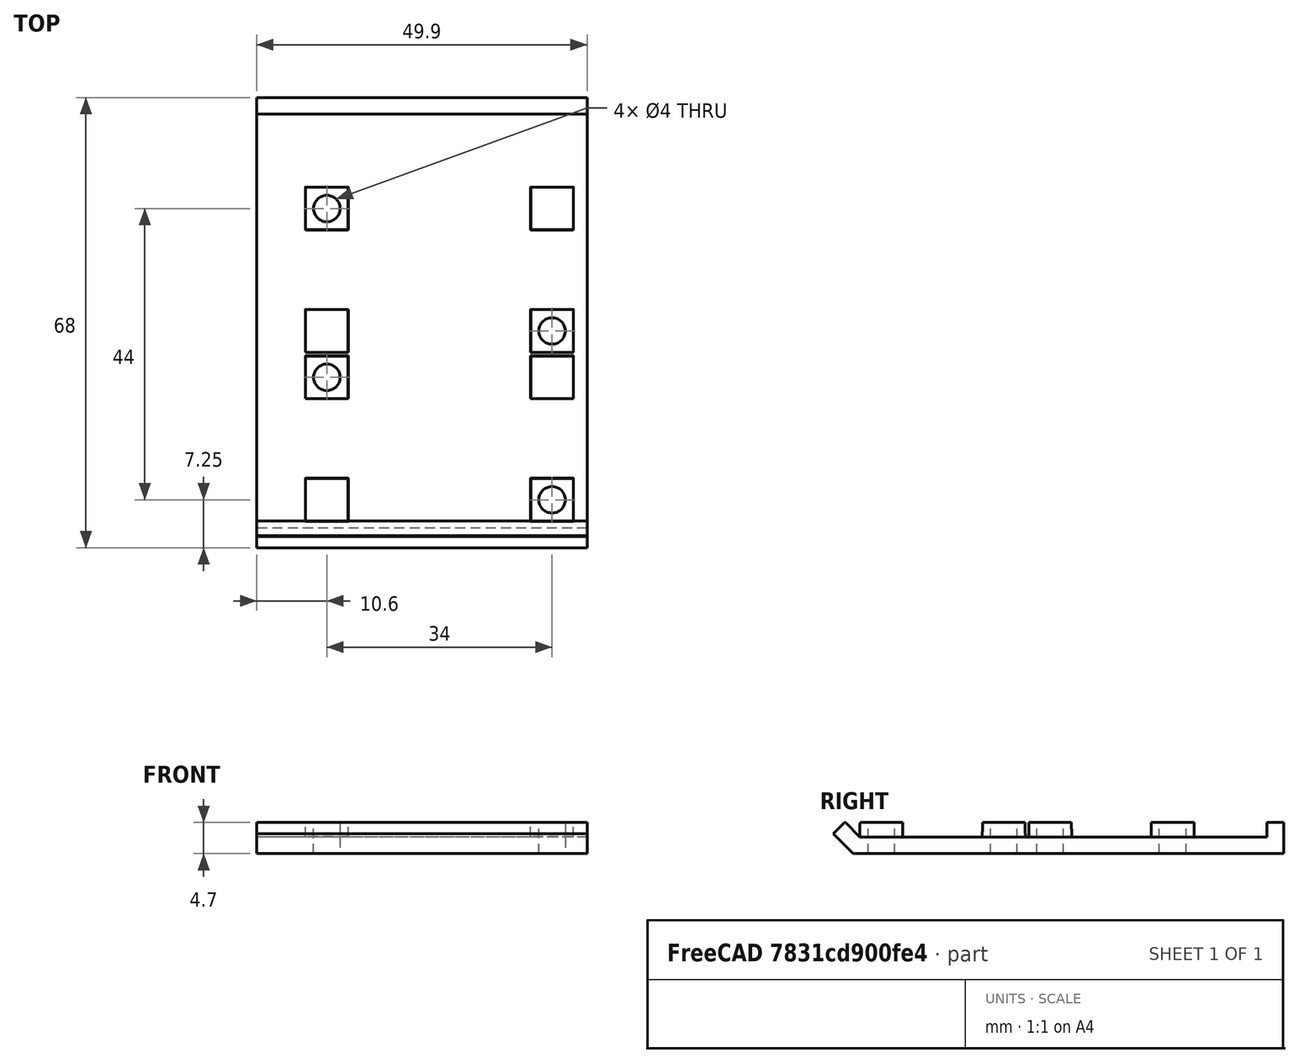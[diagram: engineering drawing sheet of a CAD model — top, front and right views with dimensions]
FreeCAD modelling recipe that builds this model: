
FCSTD DOCUMENT  (FreeCAD 0.20R29177 (Git))
Label: epreuveDCDC
License: All rights reserved
LicenseURL: http://en.wikipedia.org/wiki/All_rights_reserved
objects: Part::Box×3, Part::Cut×3, Part::Feature×1
note: 7 computed .brp shape members not serialized (recipe doc carries the construction recipe); baked Part::Feature solids carry a one-line shape summary decoded from their .brp

FEATURE [Part::Feature] Part__Feature  label="base"
  shape: bbox 85 x 68 x 63.81 mm, 243 faces (baked)
FEATURE [Part::Box] Box  label="Cube"
  AttacherType = Attacher::AttachEngine3D
  Height = 76
  Length = 23
  Placement = pos=(-14.9,-70.9,-10.3) rot=(0,0,1;0rad)
  Width = 82
FEATURE [Part::Box] Box001  label="Cube001"
  AttacherType = Attacher::AttachEngine3D
  Height = 76
  Length = 23
  Placement = pos=(-87.8,-70.9,-10.3) rot=(0,0,1;0rad)
  Width = 82
FEATURE [Part::Box] Box002  label="Cube002"
  AttacherType = Attacher::AttachEngine3D
  Height = 76
  Length = 59
  Placement = pos=(-68.9,-72.9,4.7) rot=(0,0,1;0rad)
  Width = 82
FEATURE [Part::Cut] Cut
  Base = -> Part__Feature
  Tool = -> Box
FEATURE [Part::Cut] Cut001
  Base = -> Cut
  Tool = -> Box001
FEATURE [Part::Cut] Cut002
  Base = -> Cut001
  Tool = -> Box002
